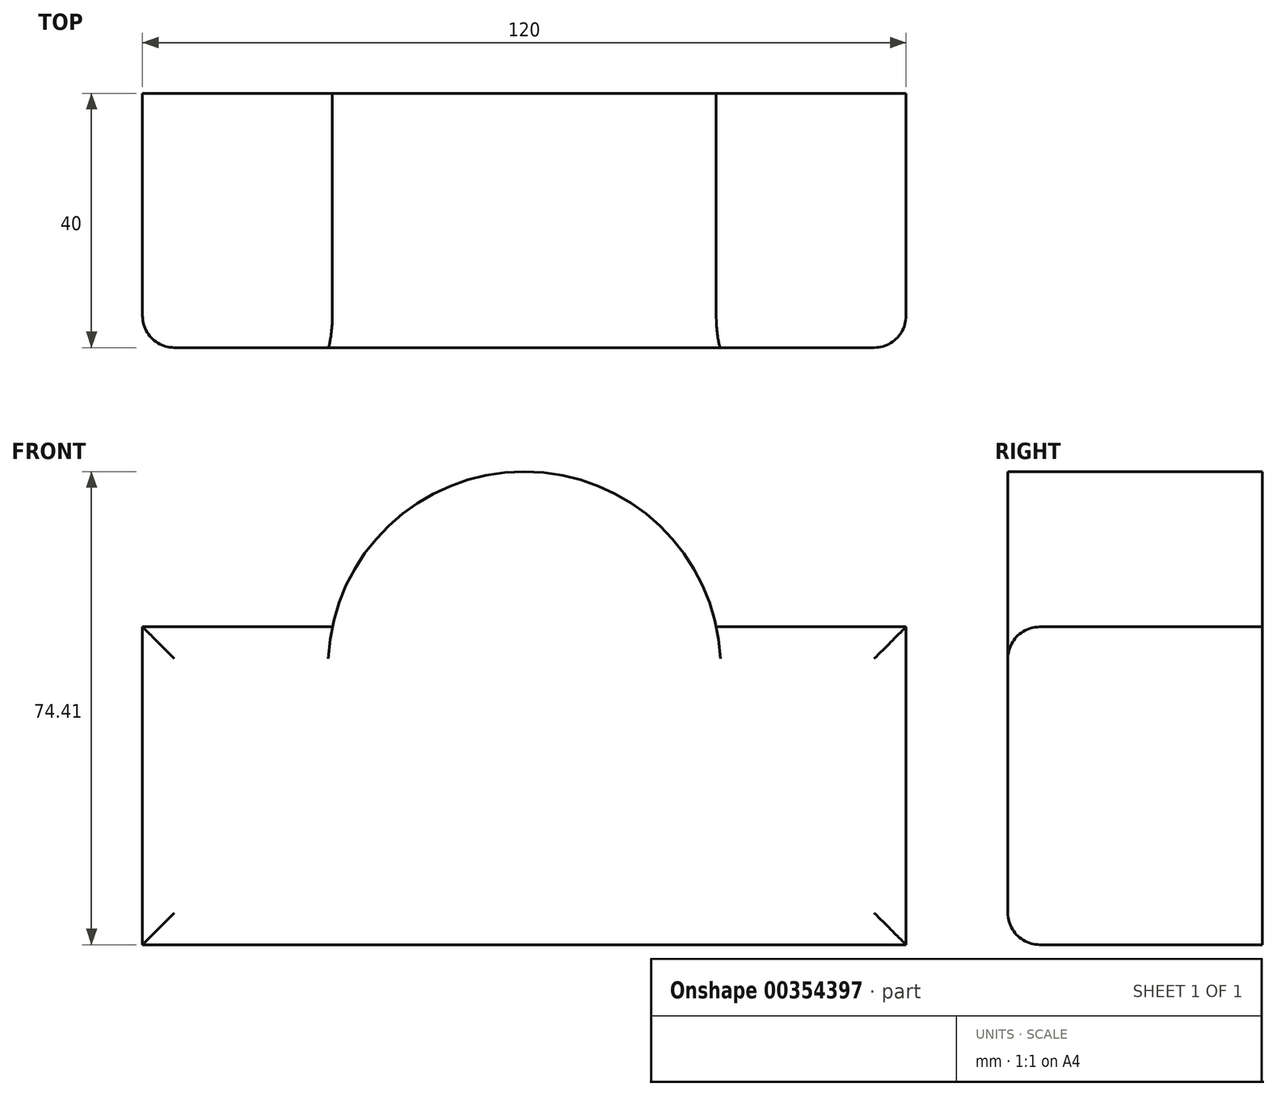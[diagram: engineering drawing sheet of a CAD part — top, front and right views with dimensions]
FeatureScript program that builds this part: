
annotation { "Feature Type Name" : "Feature", "Feature Type Description" : "" }
export const myFeature = defineFeature(function(context is Context, id is Id, definition is map)
    precondition{}
    {
        {
            var Q0;
            Q0=qCreatedBy(makeId("Front.planeOp"),FACE);
            var sketch = newSketch(context, id + "F0", { "sketchPlane" : qUnion([Q0])});
            skLineSegment(sketch, "E0.bottom", {"start": v(60, -25) * mm, "end": v(-60, -25) * mm});
            skLineSegment(sketch, "E0.top", {"start": v(60, 25) * mm, "end": v(-60, 25) * mm});
            skLineSegment(sketch, "E0.left", {"start": v(60, -25) * mm, "end": v(60, 25) * mm});
            skLineSegment(sketch, "E0.right", {"start": v(-60, -25) * mm, "end": v(-60, 25) * mm});
            skPoint(sketch, "E0.middle", {"position": v(0, 0) * mm});
            skArc(sketch, "E1", {"start": v(30.17, 25) * mm, "mid": v(0, 49.4) * mm, "end": v(-30.17, 25) * mm});
            skSolve(sketch);
        }
        {
            var Q0;
            Q0=makeQuery(id+"F0.imprint","IMPRINT",FACE,{"disambiguationData":[TD([[makeQuery(id+"F0.imprint","IMPRINT",EDGE,{"derivedFrom":sQuery(id+"F0.wireOp",EDGE,"E0.bottom")}),-1.0]])]});
            var Q1;
            {var subQ0=sQuery(id+"F0.wireOp",EDGE,"E1");Q1=makeQuery(id+"F0.imprint","IMPRINT",FACE,{"disambiguationData":[TD([[makeQuery(id+"F0.imprint","IMPRINT",EDGE,{"derivedFrom":subQ0}),1.0]])]});}
            extrude(context, id + "F1", {"entities" : qUnion([Q0, Q1]), "depth" : 40 * mm});
        }
        {
            var Q0;
            Q0=makeQuery(id+"F1.opExtrude","CAP_FACE",FACE,{"disambiguationData":[OSD([sQuery(id+"F0.wireOp",EDGE,"E0.bottom"),sQuery(id+"F0.wireOp",EDGE,"E0.top"),sQuery(id+"F0.wireOp",EDGE,"E0.left"),sQuery(id+"F0.wireOp",EDGE,"E0.right")])],"isStart":false});
            var sketch = newSketch(context, id + "F2", { "sketchPlane" : qUnion([Q0])});
            skCircle(sketch, "E2", {"center": v(0, 0) * mm, "radius": 450 * mm});
            skSolve(sketch);
        }
        {
            var Q0;
            Q0=makeQuery(id+"F2.imprint","IMPRINT",FACE,{"disambiguationData":[TD([[makeQuery(id+"F2.imprint","IMPRINT",EDGE,{"derivedFrom":sQuery(id+"F2.wireOp",EDGE,"E2")}),1.0]])]});
            extrude(context, id + "F3", {"entities" : qUnion([Q0]), "operationType" : NewBodyOperationType.REMOVE, "oppositeDirection" : true, "depth" : 25 * mm});
        }
        {
            var Q0;
            Q0=makeQuery(id+"F1.opExtrude","CAP_EDGE",EDGE,{"disambiguationData":[OSD([sQuery(id+"F0.wireOp",EDGE,"E0.right")])],"isStart":false});
            var Q1;
            Q1=makeQuery(id+"F1.opExtrude","CAP_EDGE",EDGE,{"disambiguationData":[OSD([sQuery(id+"F0.wireOp",EDGE,"E0.top")])],"isStart":false});
            var Q2;
            Q2=makeQuery(id+"F1.opExtrude","CAP_EDGE",EDGE,{"disambiguationData":[OSD([sQuery(id+"F0.wireOp",EDGE,"E0.left")])],"isStart":false});
            var Q3;
            Q3=makeQuery(id+"F1.opExtrude","CAP_EDGE",EDGE,{"disambiguationData":[OSD([sQuery(id+"F0.wireOp",EDGE,"E0.bottom")])],"isStart":false});
            var Q4;
            Q4=makeQuery(id+"F3.boolean.opBoolean","COPY",EDGE,{"derivedFrom":makeQuery(id+"F3.opExtrude","CAP_EDGE",EDGE,{"disambiguationData":[OSD([sQuery(id+"F2.wireOp",EDGE,"E2")])],"isStart":true})});
            fillet(context, id + "F4", {"entities" : qUnion([Q0, Q1, Q2, Q3, Q4]), "radius" : 5 * mm, "tangentPropagation" : true, "allowEdgeOverflow" : false});
        }
    });
